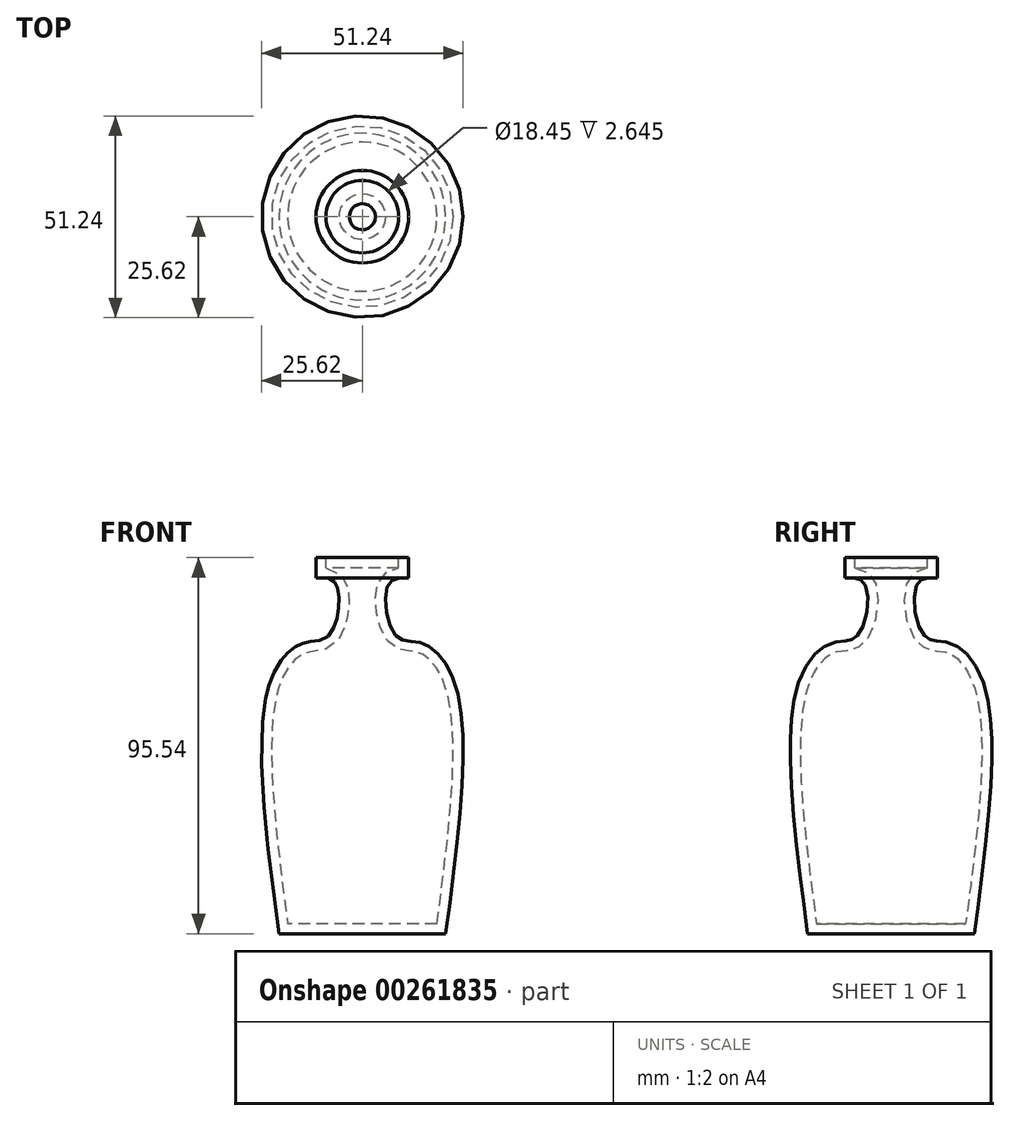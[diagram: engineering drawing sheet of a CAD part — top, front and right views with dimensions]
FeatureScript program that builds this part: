
annotation { "Feature Type Name" : "Feature", "Feature Type Description" : "" }
export const myFeature = defineFeature(function(context is Context, id is Id, definition is map)
    precondition{}
    {
        {
            var Q0;
            Q0=qCreatedBy(makeId("Front.planeOp"),FACE);
            var sketch = newSketch(context, id + "F0", { "sketchPlane" : qUnion([Q0])});
            skLineSegment(sketch, "E0", {"start": v(0, 67.07) * mm, "end": v(0, -63.54) * mm});
            skLineSegment(sketch, "E1", {"start": v(0, -57.65) * mm, "end": v(-21.18, -57.65) * mm});
            skFitSpline(sketch, "E2", {"points": [v(-21.18, -57.65) * mm, v(-23.77, 5.18) * mm, v(-14.83, 16.24) * mm, v(-8.47, 18.12) * mm, v(-6.59, 31.06) * mm, v(-11.77, 32.7) * mm], "startDerivative": vector(-25.27, 189.38) * mm, "endDerivative": vector(-54.4, -2.46) * mm});
            skLineSegment(sketch, "E3", {"start": v(-11.77, 32.7) * mm, "end": v(-11.77, 37.89) * mm});
            skLineSegment(sketch, "E4", {"start": v(-11.77, 37.89) * mm, "end": v(0, 37.89) * mm});
            skSolve(sketch);
        }
        {
            var Q0;
            {var subQ0=sQuery(id+"F0.wireOp",EDGE,"E1");Q0=makeQuery(id+"F0.imprint","IMPRINT",FACE,{"disambiguationData":[TD([[makeQuery(id+"F0.imprint","IMPRINT",EDGE,{"derivedFrom":subQ0}),-1.0]])]});}
            var Q1;
            Q1=sQuery(id+"F0.wireOp",EDGE,"E0");
            revolve(context, id + "F1", {"entities" : qUnion([Q0]), "axis" : qUnion([Q1]), "revolveType" : RevolveType.FULL});
        }
        {
            var Q0;
            Q0=makeQuery(id+"F1.opRevolve","SWEPT_FACE",FACE,{"disambiguationData":[OSD([sQuery(id+"F0.wireOp",EDGE,"E4")])]});
            shell(context, id + "F2", {"entities" : qUnion([Q0]), "thickness" : 2.54 * mm});
        }
    });
